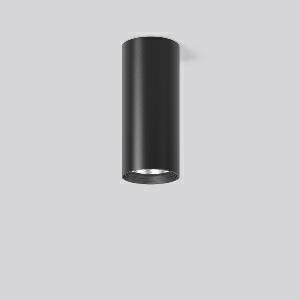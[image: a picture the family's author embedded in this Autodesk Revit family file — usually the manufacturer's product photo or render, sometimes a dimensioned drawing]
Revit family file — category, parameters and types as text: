
# Revit family: heledon_mini_a_931202_003_2_76_586e
name_source: partatom
category: Lighting Fixtures
units: mm (PartAtom-declared; Revit-internal decimal feet)

## family parameters
Cut with Voids When Loaded = No
Host = Face
Light Source = No
Part Type = Normal
Room Calculation Point = No
Round Connector Dimension = Use Diameter
Shared = No

## types (1)
- HELEDON mini A (1 x LED Modul 927, 2400 lm, 2700)
    Apparent Load = 20 VA
    Approval mark = CE
    CIE Flux Codes = 95 99 100 100 100
    Color Rendering = 92
    Color Temperature = 2700
    Default Elevation = 1800 mm
    Description = Series: HELEDON mini
Cylindrical surface-mounted downlight. Housing: die-cast aluminium, powder-coated. Internal ceiling frame polycarbonate with bayonet mounting. Black plastic ring and recessed LED to prevent glare from the side. Optical assembly with reflector made of MIRO-Silver with 98% total light reflection for outstanding efficiency - can be changed without tools. Best colour rendering index Ra>90. Suitable for Ceiling mounting. Easy installation with a separate ceiling frame with bayonet mounting and plug connection. Driver integrated. Connected via plug-in connector. High quality converter without flickering and stroboscopic effect. The following accessories can be mounted without use of tools: interchangeable lenses, decorative glasses, honeycomb louvre, clear and frosted diffusers, white interchangeable plastic ring. 
Colour: deep black, matt (RAL 9005)
Diameter: 87 mm
Height: 197 mm
Lamp: LED
Socket: without socket
Colour temperature: 2700K
Colour rendering index (CRI): 92
System power: 20 W
Rated luminous flux: 2400 lm
Luminous efficiency: 120 lm/W
Control gear: Converter, dimmable, DALI
Protection class: I
Type of protection: IP 20
    Height = 197 mm
    Lamp = 1 x LED Modul 927
    Lamp Light Flux = 2400 lm
    Lamp count = 1
    Length = 87 mm
    Lifetime = 50000 h
    Luminous efficacy = 120 lm/W
    Manufacturer = RZB
    ModVariant = No
    Model = 931202.003.2.76
    Mounting Place = Ceiling
    Mounting Type = Surface mounted
    Number of Poles = 1
    OnlyDefault = Yes
    Power Factor = 1
    Product Name = HELEDON mini A
    Product group = Surface mounted downlights
    ProductGroupID = 302
    Protection Class = Protection class I
    Protection Degree = IP 20
    RLX_Detail_Level = 1
    RLX_Emergency_Light_Flux = 0 lm
    RLX_Emergency_Type = 0
    RLX_Emergency_Type_DB = No
    RlxData = <blob elided: 106233 chars, md5=50356c75>
    Socket = socket
    Standby Power = 0 W
    System Light Flux = 2400 lm
    System Power = 20 W
    Type Comments = Product without accessories
    Type Image = 931188.003.jpg
    URL = http://relux.com
    VarID = ---
    Voltage = 230 V
    Voltage Range = 220-240 V
    Weight = 0.00 kg
    Width = 0 mm  [stored 0 ft]

note: [stored X ft] marks values corroborated as IEEE doubles in the binary element streams (Revit-internal decimal feet)

## geometry (parser evidence)
native form markers: Blend x4, Sweep x9
no freeform markers — native parametric forms only
